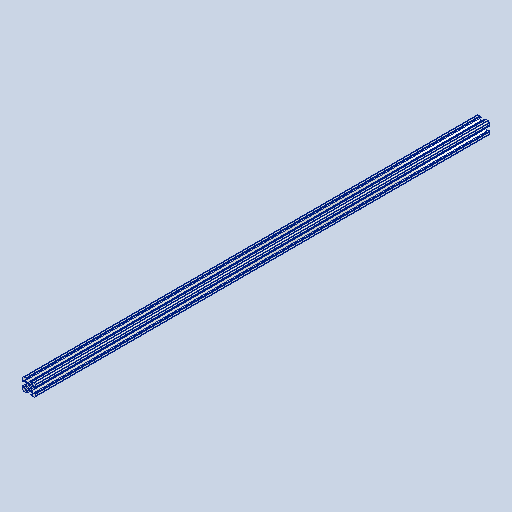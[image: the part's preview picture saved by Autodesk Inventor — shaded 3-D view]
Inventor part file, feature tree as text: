
AUTODESK INVENTOR PART (.ipt)
format: ipt  version: 2023 (Build 270158000, 158)  size: 326,144 bytes
history: native  units: in
note: dims shown in document units (in); Inventor stores cm internally (conversion verified against a paired STEP export)
features: extrude x1, sketch x1, projected_geometry x1, other x1
ambient origin geometry x8: Origin, YZ Plane, XZ Plane, XY Plane, X Axis, Y Axis, Z Axis, Center Point
bodies: Solid1 (feature_tree)
feature tree (4):
  extrude  "Extrusion1"  [1 undecoded]
  sketch  "Sketch1"  dims[d0=24.0in d1=0.0in]
  projected_geometry  "Projected Loop1"
  other  "Boss-Extrude1"
note: 1 required parameter value undecoded (feature->parameter linkage not recoverable at this tier; creation-order binding heuristic only, values carry confidence <= 0.55)
